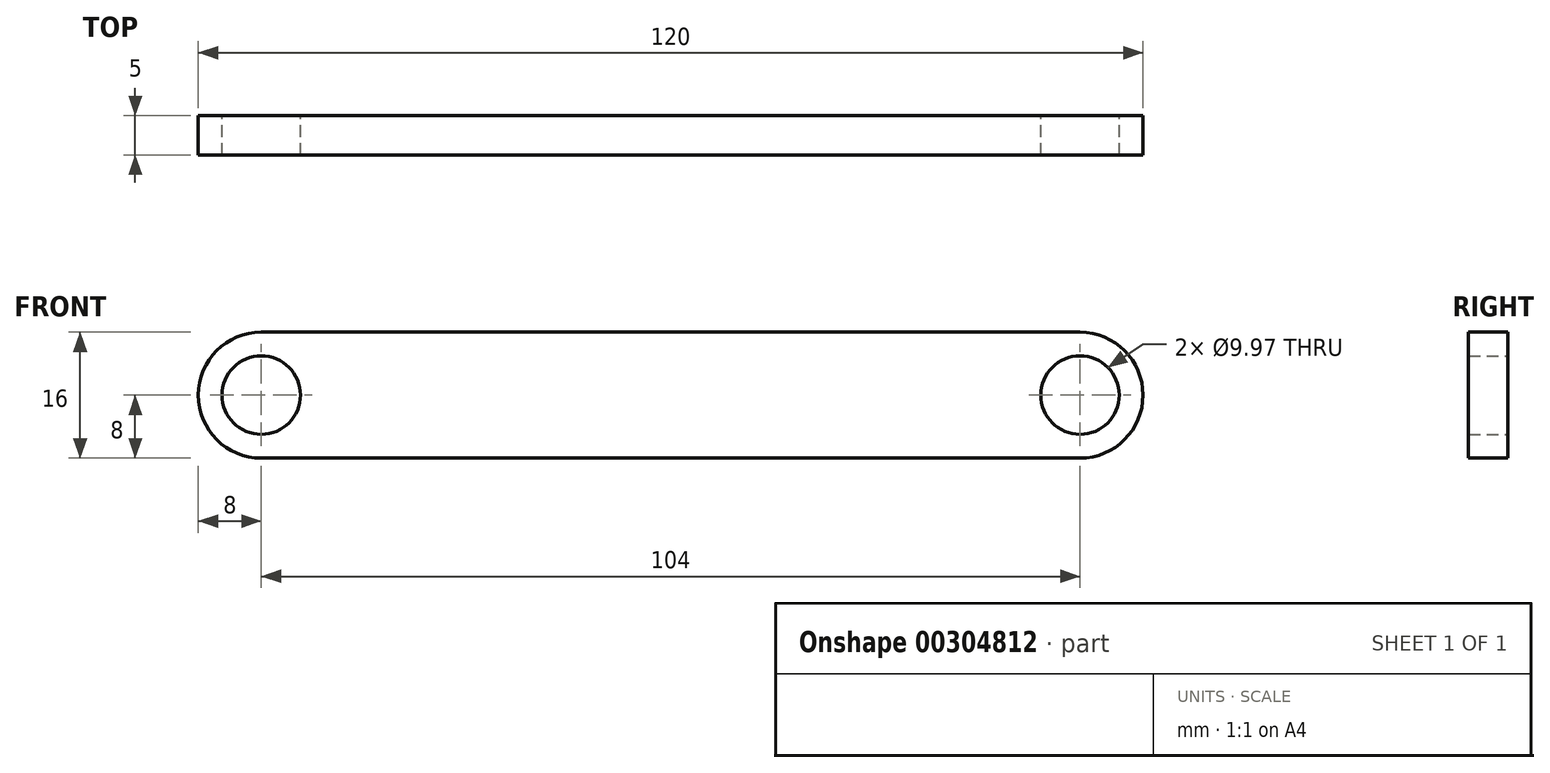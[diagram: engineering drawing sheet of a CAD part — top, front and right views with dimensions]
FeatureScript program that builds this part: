
annotation { "Feature Type Name" : "Feature", "Feature Type Description" : "" }
export const myFeature = defineFeature(function(context is Context, id is Id, definition is map)
    precondition{}
    {
        {
            var Q0;
            Q0=qCreatedBy(makeId("Front.planeOp"),FACE);
            var sketch = newSketch(context, id + "F0", { "sketchPlane" : qUnion([Q0])});
            skLineSegment(sketch, "E0.bottom", {"start": v(52, -8) * mm, "end": v(-52, -8) * mm});
            skLineSegment(sketch, "E0.top", {"start": v(52, 8) * mm, "end": v(-52, 8) * mm});
            skLineSegment(sketch, "E0.left", {"start": v(60, 0) * mm, "end": v(60, 0) * mm});
            skLineSegment(sketch, "E0.right", {"start": v(-60, 0) * mm, "end": v(-60, 0) * mm});
            skPoint(sketch, "E0.middle", {"position": v(0, 0) * mm});
            skCircle(sketch, "E1", {"center": v(-52, 0) * mm, "radius": 4.99 * mm});
            skCircle(sketch, "E2.MirrorC", {"center": v(52, 0) * mm, "radius": 4.99 * mm});
            skPoint(sketch, "E3.visualSharp", {"position": v(-60, 8) * mm});
            skArc(sketch, "E3.filletArc", {"start": v(-52, 8) * mm, "mid": v(-57.66, 5.66) * mm, "end": v(-60, 0) * mm});
            skPoint(sketch, "E4.visualSharp", {"position": v(-60, -8) * mm});
            skArc(sketch, "E4.filletArc", {"start": v(-60, 0) * mm, "mid": v(-57.66, -5.66) * mm, "end": v(-52, -8) * mm});
            skPoint(sketch, "E5.visualSharp", {"position": v(60, 8) * mm});
            skArc(sketch, "E5.filletArc", {"start": v(60, 0) * mm, "mid": v(57.66, 5.66) * mm, "end": v(52, 8) * mm});
            skPoint(sketch, "E6.visualSharp", {"position": v(60, -8) * mm});
            skArc(sketch, "E6.filletArc", {"start": v(52, -8) * mm, "mid": v(57.66, -5.66) * mm, "end": v(60, 0) * mm});
            skSolve(sketch);
        }
        {
            var Q0;
            Q0=makeQuery(id+"F0.imprint","IMPRINT",FACE,{"disambiguationData":[TD([[makeQuery(id+"F0.imprint","IMPRINT",EDGE,{"derivedFrom":sQuery(id+"F0.wireOp",EDGE,"E0.bottom")}),-1.0]])]});
            extrude(context, id + "F1", {"entities" : qUnion([Q0]), "depth" : 5 * mm});
        }
    });
